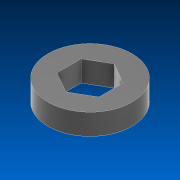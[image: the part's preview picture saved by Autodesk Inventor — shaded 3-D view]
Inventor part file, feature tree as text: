
AUTODESK INVENTOR PART (.ipt)
format: ipt  version: 2022.2 (Build 262287000, 287)  size: 90,624 bytes
history: native  units: in
note: dims shown in document units (in); Inventor stores cm internally (conversion verified against a paired STEP export)
features: extrude x1, sketch x1
ambient origin geometry x8: Origin, YZ Plane, XZ Plane, XY Plane, X Axis, Y Axis, Z Axis, Center Point
bodies: Solid1 (feature_tree)
feature tree (2):
  extrude  "Extrusion1"  Depth=0.125in
  sketch  "Sketch1"  dims[d0=0.25in d1=0.5in d2=0.125in d3=0.0in]
